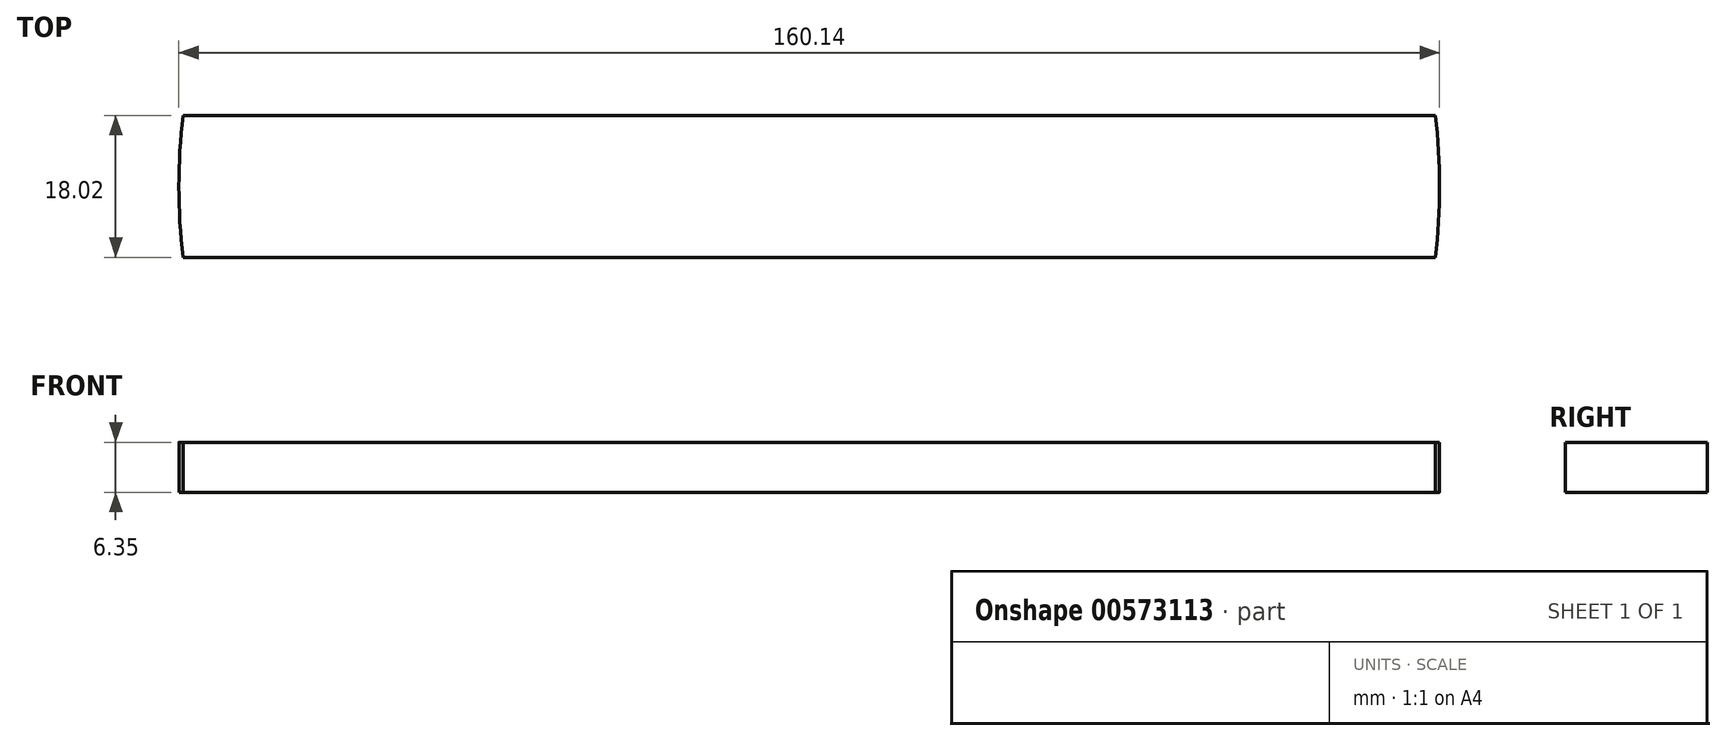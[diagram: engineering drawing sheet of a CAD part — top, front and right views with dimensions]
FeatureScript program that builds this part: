
annotation { "Feature Type Name" : "Feature", "Feature Type Description" : "" }
export const myFeature = defineFeature(function(context is Context, id is Id, definition is map)
    precondition{}
    {
        {
            var Q0;
            Q0=qCreatedBy(makeId("Top.planeOp"),FACE);
            var sketch = newSketch(context, id + "F0", { "sketchPlane" : qUnion([Q0])});
            skArc(sketch, "E0", {"start": v(-79.56, 9.01) * mm, "mid": v(-80.07, 0) * mm, "end": v(-79.56, -9.01) * mm});
            skLineSegment(sketch, "E1", {"start": v(0, 9.01) * mm, "end": v(-79.56, 9.01) * mm});
            skLineSegment(sketch, "E2", {"start": v(0, 9.01) * mm, "end": v(79.56, 9.01) * mm});
            skLineSegment(sketch, "E3", {"start": v(0, -9.01) * mm, "end": v(79.56, -9.01) * mm});
            skLineSegment(sketch, "E4", {"start": v(0, -9.01) * mm, "end": v(-79.56, -9.01) * mm});
            skArc(sketch, "E5.trimOffspring", {"start": v(79.56, -9.01) * mm, "mid": v(80.07, 0) * mm, "end": v(79.56, 9.01) * mm});
            skPoint(sketch, "E6.orphan", {"position": v(-80.07, 0) * mm});
            skSolve(sketch);
        }
        {
            var Q0;
            Q0 = qSketchRegion(id + "F0", true);
            extrude(context, id + "F1", {"entities" : qUnion([Q0]), "depth" : 6.35 * mm, "offsetDistance" : 25.4 * mm});
        }
    });
